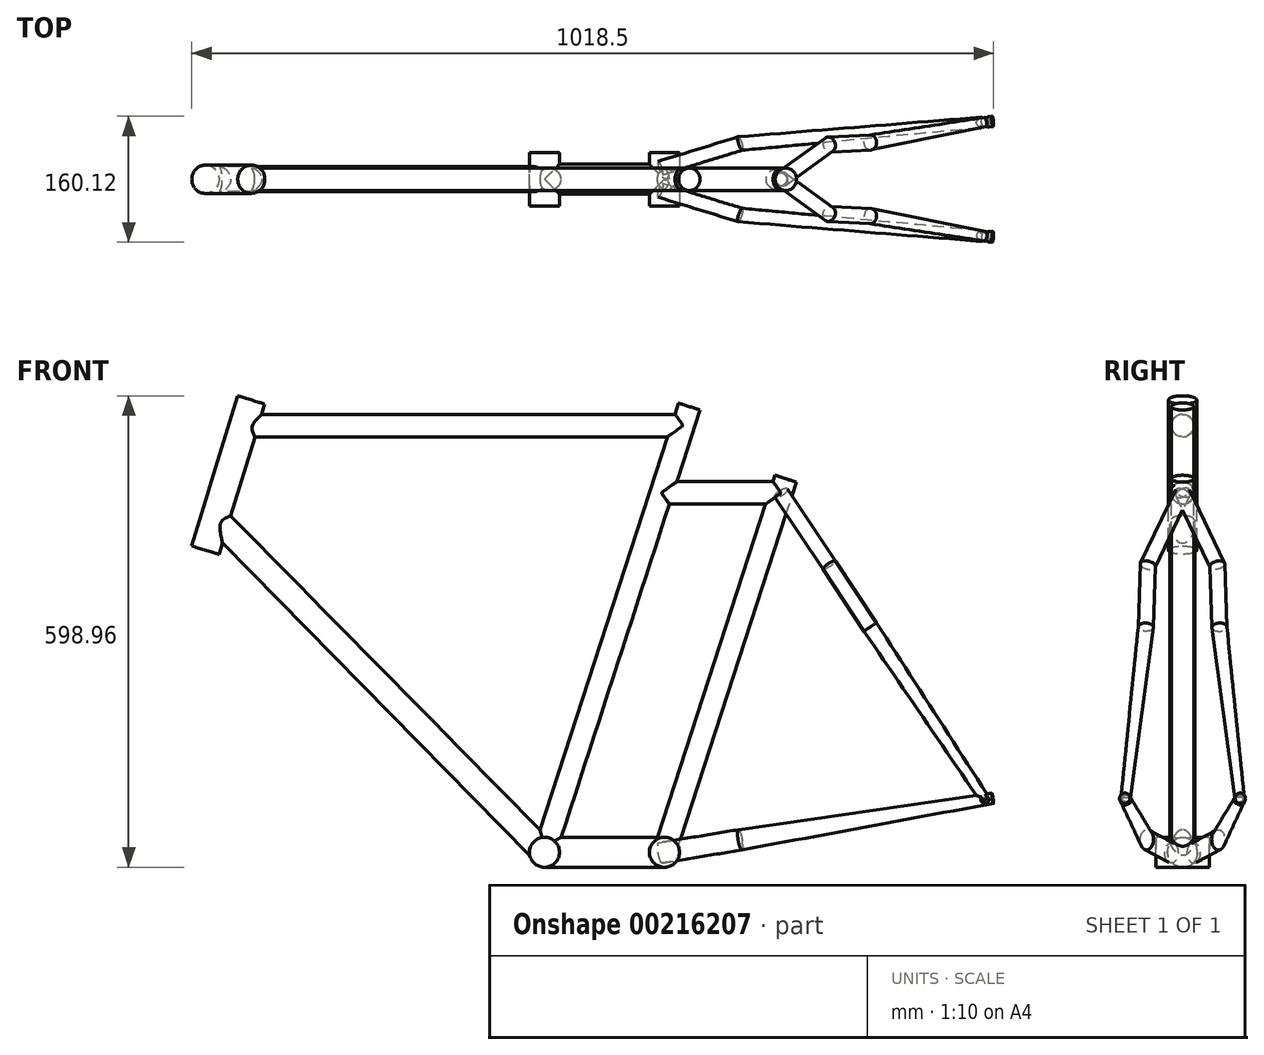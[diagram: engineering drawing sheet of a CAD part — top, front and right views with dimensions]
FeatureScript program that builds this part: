
annotation { "Feature Type Name" : "Feature", "Feature Type Description" : "" }
export const myFeature = defineFeature(function(context is Context, id is Id, definition is map)
    precondition{}
    {
        {
            var Q0;
            Q0=qCreatedBy(makeId("Front.planeOp"),FACE);
            var sketch = newSketch(context, id + "F0", { "sketchPlane" : qUnion([Q0])});
            skLineSegment(sketch, "E0", {"start": v(0, 0) * mm, "end": v(176.14, 542.1) * mm});
            skLineSegment(sketch, "E1", {"start": v(-382.35, 542.09) * mm, "end": v(-527.6, 67) * mm, "construction": true});
            skLineSegment(sketch, "E2.0", {"start": v(1276.12, 67) * mm, "end": v(-807.18, 67) * mm, "construction": true});
            skLineSegment(sketch, "E3", {"start": v(-372.4, 574.65) * mm, "end": v(-430.75, 383.8) * mm});
            skLineSegment(sketch, "E4", {"start": v(0, 0) * mm, "end": v(-418.23, 424.73) * mm});
            skLineSegment(sketch, "E5", {"start": v(300.73, 456.5) * mm, "end": v(152.4, 0) * mm});
            skLineSegment(sketch, "E6", {"start": v(0, 0) * mm, "end": v(152.4, 0) * mm});
            skLineSegment(sketch, "E7", {"start": v(-530.74, -257.5) * mm, "end": v(-876.38, -257.5) * mm, "construction": true});
            skLineSegment(sketch, "E8", {"start": v(-527.6, 67) * mm, "end": v(-626.81, -257.5) * mm});
            skLineSegment(sketch, "E9", {"start": v(-626.81, -257.5) * mm, "end": v(-586.81, -257.5) * mm});
            skLineSegment(sketch, "E10", {"start": v(-586.81, -257.5) * mm, "end": v(-577.2, 67) * mm});
            skPoint(sketch, "E10.endSnap0", {"position": v(-577.2, -95.25) * mm});
            skCircle(sketch, "E11", {"center": v(-577.2, 67) * mm, "radius": 324.63 * mm});
            skLineSegment(sketch, "E12", {"start": v(-577.2, 67) * mm, "end": v(-531.84, 53.13) * mm});
            skCircle(sketch, "E13", {"center": v(559.48, 67) * mm, "radius": 324.63 * mm});
            skLineSegment(sketch, "E14", {"start": v(152.4, 0) * mm, "end": v(559.48, 67) * mm});
            skLineSegment(sketch, "E15", {"start": v(300.73, 456.5) * mm, "end": v(559.48, 67) * mm});
            skLineSegment(sketch, "E16", {"start": v(-382.35, 542.09) * mm, "end": v(176.14, 542.1) * mm});
            skLineSegment(sketch, "E17", {"start": v(300.73, 456.5) * mm, "end": v(148.33, 456.5) * mm});
            skSolve(sketch);
        }
        {
            var Q0;
            Q0=qCreatedBy(makeId("Front.planeOp"),FACE);
            cPlane(context, id + "F1", {"entities" : qUnion([Q0]), "cplaneType" : CPlaneType.OFFSET, "offset" : 34 * mm, "width" : 152.4 * mm, "height" : 152.4 * mm});
        }
        {
            var Q0;
            Q0=qCreatedBy(id+"F1.planeOp",FACE);
            var sketch = newSketch(context, id + "F2", { "sketchPlane" : qUnion([Q0])});
            skCircle(sketch, "E18", {"center": v(0, 0) * mm, "radius": 19.05 * mm});
            skSolve(sketch);
        }
        {
            var Q0;
            Q0=makeQuery(id+"F2.imprint","IMPRINT",FACE,{"disambiguationData":[TD([[makeQuery(id+"F2.imprint","IMPRINT",EDGE,{"derivedFrom":sQuery(id+"F2.wireOp",EDGE,"E18")}),1.0]])]});
            extrude(context, id + "F3", {"entities" : qUnion([Q0]), "oppositeDirection" : true, "depth" : 68 * mm});
        }
        {
            var Q0;
            Q0=qCreatedBy(makeId("Right.planeOp"),FACE);
            var sketch = newSketch(context, id + "F4", { "sketchPlane" : qUnion([Q0])});
            skCircle(sketch, "E19", {"center": v(0, 0) * mm, "radius": 19.05 * mm});
            skSolve(sketch);
        }
        {
            var Q0;
            Q0=qCreatedBy(id+"F1.planeOp",FACE);
            var sketch = newSketch(context, id + "F5", { "sketchPlane" : qUnion([Q0])});
            skCircle(sketch, "E20", {"center": v(152.4, 0) * mm, "radius": 19.05 * mm});
            skSolve(sketch);
        }
        {
            var Q0;
            Q0=makeQuery(id+"F4.imprint","IMPRINT",FACE,{"disambiguationData":[TD([[makeQuery(id+"F4.imprint","IMPRINT",EDGE,{"derivedFrom":sQuery(id+"F4.wireOp",EDGE,"E19")}),1.0]])]});
            var Q1;
            Q1=makeQuery(id+"F7.opExtrude","SWEPT_BODY",BODY,{"disambiguationData":[OSD([sQuery(id+"F5.wireOp",EDGE,"E20")])]});
            extrude(context, id + "F6", {"entities" : qUnion([Q0]), "operationType" : NewBodyOperationType.ADD, "endBoundEntityBody" : qUnion([Q1]), "depth" : 154 * mm});
        }
        {
            var Q0;
            Q0=makeQuery(id+"F5.imprint","IMPRINT",FACE,{"disambiguationData":[TD([[makeQuery(id+"F5.imprint","IMPRINT",EDGE,{"derivedFrom":sQuery(id+"F5.wireOp",EDGE,"E20")}),1.0]])]});
            extrude(context, id + "F7", {"entities" : qUnion([Q0]), "operationType" : NewBodyOperationType.ADD, "oppositeDirection" : true, "depth" : 68 * mm});
        }
        {
            var Q0;
            Q0=sQuery(id+"F0.wireOp",EDGE,"E0");
            var Q1;
            Q1=sQuery(id+"F0.wireOp",VERTEX,"E0.end");
            cPlane(context, id + "F8", {"entities" : qUnion([Q0, Q1]), "cplaneType" : CPlaneType.LINE_POINT, "offset" : 152.4 * mm, "width" : 152.4 * mm, "height" : 152.4 * mm});
        }
        {
            var Q0;
            Q0=qCreatedBy(id+"F8.planeOp",FACE);
            var sketch = newSketch(context, id + "F9", { "sketchPlane" : qUnion([Q0])});
            skCircle(sketch, "E21", {"center": v(0, 0) * mm, "radius": 14.3 * mm});
            skSolve(sketch);
        }
        {
            var Q0;
            Q0=makeQuery(id+"F9.imprint","IMPRINT",FACE,{"disambiguationData":[TD([[makeQuery(id+"F9.imprint","IMPRINT",EDGE,{"derivedFrom":sQuery(id+"F9.wireOp",EDGE,"E21")}),1.0]])]});
            var Q1;
            Q1=makeQuery(id+"F3.opExtrude","SWEPT_BODY",BODY,{"disambiguationData":[OSD([sQuery(id+"F2.wireOp",EDGE,"E18")])]});
            extrude(context, id + "F10", {"entities" : qUnion([Q0]), "operationType" : NewBodyOperationType.ADD, "endBound" : BoundingType.UP_TO_BODY, "oppositeDirection" : true, "endBoundEntityBody" : qUnion([Q1]), "depth" : 25.4 * mm, "hasSecondDirection" : true, "secondDirectionOppositeDirection" : false, "secondDirectionDepth" : 25.4 * mm});
        }
        {
            var Q0;
            Q0=sQuery(id+"F0.wireOp",EDGE,"E14");
            cPlane(context, id + "F11", {"entities" : qUnion([Q0]), "cplaneType" : CPlaneType.LINE_ANGLE, "offset" : 152.4 * mm, "angle" : 90 * degree, "width" : 152.4 * mm, "height" : 152.4 * mm});
        }
        {
            var Q0;
            Q0=qCreatedBy(id+"F11.planeOp",FACE);
            var sketch = newSketch(context, id + "F12", { "sketchPlane" : qUnion([Q0])});
            skLineSegment(sketch, "E22", {"start": v(562.93, 0) * mm, "end": v(562.93, -72.5) * mm});
            skLineSegment(sketch, "E23", {"start": v(562.93, -72.5) * mm, "end": v(247.86, -45.41) * mm});
            skLineSegment(sketch, "E24", {"start": v(247.86, -45.41) * mm, "end": v(145.11, -14.17) * mm});
            skSolve(sketch);
        }
        {
            var Q0;
            Q0=sQuery(id+"F12.wireOp",EDGE,"E23");
            var Q1;
            Q1=sQuery(id+"F12.wireOp",VERTEX,"E23.start");
            cPlane(context, id + "F13", {"entities" : qUnion([Q0, Q1]), "cplaneType" : CPlaneType.LINE_POINT, "offset" : 152.4 * mm, "width" : 152.4 * mm, "height" : 152.4 * mm});
        }
        {
            var Q0;
            Q0=qCreatedBy(id+"F13.planeOp",FACE);
            var sketch = newSketch(context, id + "F14", { "sketchPlane" : qUnion([Q0])});
            skCircle(sketch, "E25", {"center": v(24.02, -24.75) * mm, "radius": 6.73 * mm});
            skSolve(sketch);
        }
        {
            var Q0;
            Q0=sQuery(id+"F12.wireOp",EDGE,"E24");
            var Q1;
            Q1=sQuery(id+"F12.wireOp",VERTEX,"E24.end");
            cPlane(context, id + "F15", {"entities" : qUnion([Q0, Q1]), "cplaneType" : CPlaneType.LINE_POINT, "offset" : 152.4 * mm, "width" : 152.4 * mm, "height" : 152.4 * mm});
        }
        {
            var Q0;
            Q0=qCreatedBy(id+"F15.planeOp",FACE);
            var sketch = newSketch(context, id + "F16", { "sketchPlane" : qUnion([Q0])});
            skEllipse(sketch, "E26", {"center": v(-28.66, -24.75) * mm, "majorRadius": 13.03 * mm, "minorRadius": 8.94 * mm, "majorAxis": v(0, -1)});
            skSolve(sketch);
        }
        {
            var Q0;
            Q0=makeQuery(id+"F16.imprint","IMPRINT",FACE,{"disambiguationData":[TD([[makeQuery(id+"F16.imprint","IMPRINT",EDGE,{"derivedFrom":sQuery(id+"F16.wireOp",EDGE,"E26")}),1.0]])]});
            var Q1;
            Q1=sQuery(id+"F12.wireOp",EDGE,"E24");
            sweep(context, id + "F17", {"profiles" : qUnion([Q0]), "path" : qUnion([Q1])});
        }
        {
            var Q0;
            Q0=qCreatedBy(id+"F11.planeOp",FACE);
            var sketch = newSketch(context, id + "F18", { "sketchPlane" : qUnion([Q0])});
            skLineSegment(sketch, "E27", {"start": v(245.26, -53.97) * mm, "end": v(562.35, -79.2) * mm});
            skSolve(sketch);
        }
        {
            var Q1;
            Q1=makeQuery(id+"F17.opSweep","CAP_FACE",FACE,{"disambiguationData":[OSD([sQuery(id+"F12.wireOp",VERTEX,"E24.start"),sQuery(id+"F16.wireOp",EDGE,"E26")])],"isStart":false});
            var Q2;
            Q2=makeQuery(id+"F14.imprint","IMPRINT",FACE,{"disambiguationData":[TD([[makeQuery(id+"F14.imprint","IMPRINT",EDGE,{"derivedFrom":sQuery(id+"F14.wireOp",EDGE,"E25")}),1.0]])]});
            var Q3;
            Q3=sQuery(id+"F18.wireOp",EDGE,"E27");
            loft(context, id + "F19", {"operationType" : NewBodyOperationType.ADD, "addGuides" : true, "sheetProfilesArray" : [{ "sheetProfileEntities" : qUnion([Q1]) }, { "sheetProfileEntities" : qUnion([Q2]) }], "guidesArray" : [{ "guideEntities" : qUnion([Q3]), "guideDerivativeType" : LoftGuideDerivativeType.DEFAULT, "guideDerivativeMagnitude" : 1 }]});
        }
        {
            var Q0;
            Q0=makeQuery(id+"F19.opLoft","CAP_FACE",FACE,{"disambiguationData":[OSD([makeQuery(id+"F14.imprint","IMPRINT",FACE,{"disambiguationData":[TD([[makeQuery(id+"F14.imprint","IMPRINT",EDGE,{"derivedFrom":sQuery(id+"F14.wireOp",EDGE,"E25")}),1.0]])]})])],"isStart":true});
            extrude(context, id + "F20", {"entities" : qUnion([Q0]), "operationType" : NewBodyOperationType.ADD, "depth" : 10 * mm});
        }
        {
            var Q0;
            Q0=qCreatedBy(makeId("Front.planeOp"),FACE);
            var sketch = newSketch(context, id + "F21", { "sketchPlane" : qUnion([Q0])});
            skCircle(sketch, "E28", {"center": v(559.48, 67) * mm, "radius": 5 * mm});
            skSolve(sketch);
        }
        {
            var Q0;
            Q0=makeQuery(id+"F21.imprint","IMPRINT",FACE,{"disambiguationData":[TD([[makeQuery(id+"F21.imprint","IMPRINT",EDGE,{"derivedFrom":sQuery(id+"F21.wireOp",EDGE,"E28")}),1.0]])]});
            var Q1;
            Q1=sQuery(id+"F21.wireOp",EDGE,"E28");
            extrude(context, id + "F22", {"entities" : qUnion([Q0]), "surfaceEntities" : qUnion([Q1]), "depth" : 84.17 * mm});
        }
        {
            var Q0;
            Q0=makeQuery(id+"F22.opExtrude","SWEPT_BODY",BODY,{"disambiguationData":[OSD([sQuery(id+"F21.wireOp",EDGE,"E28")])]});
            var Q1;
            Q1=makeQuery(id+"F17.opSweep","SWEPT_BODY",BODY,{"disambiguationData":[OSD([sQuery(id+"F12.wireOp",EDGE,"E24"),sQuery(id+"F16.wireOp",EDGE,"E26")])]});
            booleanBodies(context, id + "F23", {"operationType" : BooleanOperationType.SUBTRACTION, "tools" : qUnion([Q0]), "targets" : qUnion([Q1])});
        }
        {
            var Q0;
            Q0=sQuery(id+"F0.wireOp",EDGE,"E5");
            var Q1;
            Q1=sQuery(id+"F0.wireOp",VERTEX,"E15.start");
            cPlane(context, id + "F24", {"entities" : qUnion([Q0, Q1]), "cplaneType" : CPlaneType.LINE_POINT, "offset" : 152.4 * mm, "width" : 152.4 * mm, "height" : 152.4 * mm});
        }
        {
            var Q0;
            Q0=qCreatedBy(id+"F24.planeOp",FACE);
            var sketch = newSketch(context, id + "F25", { "sketchPlane" : qUnion([Q0])});
            skCircle(sketch, "E29", {"center": v(144.94, 0) * mm, "radius": 14.3 * mm});
            skSolve(sketch);
        }
        {
            var Q0;
            Q0=makeQuery(id+"F25.imprint","IMPRINT",FACE,{"disambiguationData":[TD([[makeQuery(id+"F25.imprint","IMPRINT",EDGE,{"derivedFrom":sQuery(id+"F25.wireOp",EDGE,"E29")}),1.0]])]});
            var Q1;
            Q1=makeQuery(id+"F3.opExtrude","SWEPT_BODY",BODY,{"disambiguationData":[OSD([sQuery(id+"F2.wireOp",EDGE,"E18")])]});
            extrude(context, id + "F26", {"entities" : qUnion([Q0]), "operationType" : NewBodyOperationType.ADD, "endBound" : BoundingType.UP_TO_BODY, "endBoundEntityBody" : qUnion([Q1]), "depth" : 25.4 * mm, "hasSecondDirection" : true, "secondDirectionOppositeDirection" : true, "secondDirectionDepth" : 19 * mm});
        }
        {
            var Q0;
            Q0=sQuery(id+"F0.wireOp",EDGE,"E4");
            var Q1;
            Q1=sQuery(id+"F0.wireOp",VERTEX,"E4.end");
            cPlane(context, id + "F27", {"entities" : qUnion([Q0, Q1]), "cplaneType" : CPlaneType.LINE_POINT, "offset" : 152.4 * mm, "width" : 152.4 * mm, "height" : 152.4 * mm});
        }
        {
            var Q0;
            Q0=qCreatedBy(id+"F27.planeOp",FACE);
            var sketch = newSketch(context, id + "F28", { "sketchPlane" : qUnion([Q0])});
            skCircle(sketch, "E30", {"center": v(0, 0) * mm, "radius": 15.9 * mm});
            skSolve(sketch);
        }
        {
            var Q0;
            Q0=makeQuery(id+"F28.imprint","IMPRINT",FACE,{"disambiguationData":[TD([[makeQuery(id+"F28.imprint","IMPRINT",EDGE,{"derivedFrom":sQuery(id+"F28.wireOp",EDGE,"E30")}),1.0]])]});
            var Q1;
            Q1=makeQuery(id+"F3.opExtrude","SWEPT_BODY",BODY,{"disambiguationData":[OSD([sQuery(id+"F2.wireOp",EDGE,"E18")])]});
            extrude(context, id + "F29", {"entities" : qUnion([Q0]), "operationType" : NewBodyOperationType.ADD, "endBound" : BoundingType.UP_TO_BODY, "oppositeDirection" : true, "endBoundEntityBody" : qUnion([Q1]), "depth" : 25.4 * mm});
        }
        {
            var Q0;
            Q0=sQuery(id+"F0.wireOp",EDGE,"E3");
            var Q1;
            Q1=sQuery(id+"F0.wireOp",VERTEX,"E3.start");
            cPlane(context, id + "F30", {"entities" : qUnion([Q0, Q1]), "cplaneType" : CPlaneType.LINE_POINT, "offset" : 152.4 * mm, "width" : 152.4 * mm, "height" : 152.4 * mm});
        }
        {
            var Q0;
            Q0=qCreatedBy(id+"F30.planeOp",FACE);
            var sketch = newSketch(context, id + "F31", { "sketchPlane" : qUnion([Q0])});
            skCircle(sketch, "E31", {"center": v(-524.14, 0) * mm, "radius": 18 * mm});
            skSolve(sketch);
        }
        {
            var Q0;
            Q0=sQuery(id+"F0.wireOp",EDGE,"E15");
            cPlane(context, id + "F32", {"entities" : qUnion([Q0]), "cplaneType" : CPlaneType.LINE_ANGLE, "offset" : 152.4 * mm, "angle" : 0 * degree, "width" : 152.4 * mm, "height" : 152.4 * mm});
        }
        {
            var Q0;
            Q0=qCreatedBy(id+"F32.planeOp",FACE);
            var sketch = newSketch(context, id + "F33", { "sketchPlane" : qUnion([Q0])});
            skLineSegment(sketch, "E32", {"start": v(72.5, -253.77) * mm, "end": v(46.8, 9.14) * mm});
            skLineSegment(sketch, "E33", {"start": v(46.8, 9.14) * mm, "end": v(44.18, 103.87) * mm});
            skLineSegment(sketch, "E34", {"start": v(44.18, 103.87) * mm, "end": v(0, 213.85) * mm});
            skSolve(sketch);
        }
        {
            var Q0;
            Q0=sQuery(id+"F33.wireOp",EDGE,"E34");
            var Q1;
            Q1=sQuery(id+"F33.wireOp",VERTEX,"E34.end");
            cPlane(context, id + "F34", {"entities" : qUnion([Q0, Q1]), "cplaneType" : CPlaneType.LINE_POINT, "offset" : 152.4 * mm, "width" : 152.4 * mm, "height" : 152.4 * mm});
        }
        {
            var Q0;
            Q0=qCreatedBy(id+"F34.planeOp",FACE);
            var sketch = newSketch(context, id + "F35", { "sketchPlane" : qUnion([Q0])});
            skCircle(sketch, "E35", {"center": v(469.2, -198.29) * mm, "radius": 9.53 * mm});
            skSolve(sketch);
        }
        {
            var Q0;
            Q0=makeQuery(id+"F35.imprint","IMPRINT",FACE,{"disambiguationData":[TD([[makeQuery(id+"F35.imprint","IMPRINT",EDGE,{"derivedFrom":sQuery(id+"F35.wireOp",EDGE,"E35")}),1.0]])]});
            var Q1;
            Q1=sQuery(id+"F33.wireOp",EDGE,"E34");
            var Q2;
            Q2=sQuery(id+"F33.wireOp",EDGE,"E33");
            sweep(context, id + "F36", {"profiles" : qUnion([Q0]), "path" : qUnion([Q1, Q2])});
        }
        {
            var Q0;
            Q0=sQuery(id+"F33.wireOp",VERTEX,"E32.start");
            var Q1;
            Q1=sQuery(id+"F33.wireOp",EDGE,"E32");
            cPlane(context, id + "F37", {"entities" : qUnion([Q0, Q1]), "cplaneType" : CPlaneType.LINE_POINT, "offset" : 152.4 * mm, "width" : 152.4 * mm, "height" : 152.4 * mm});
        }
        {
            var Q0;
            Q0=qCreatedBy(id+"F37.planeOp",FACE);
            var sketch = newSketch(context, id + "F38", { "sketchPlane" : qUnion([Q0])});
            skCircle(sketch, "E36", {"center": v(498.99, -79.82) * mm, "radius": 6 * mm});
            skSolve(sketch);
        }
        {
            var Q1;
            Q1=makeQuery(id+"F36.opSweep","CAP_FACE",FACE,{"disambiguationData":[OSD([sQuery(id+"F33.wireOp",VERTEX,"E33.start"),sQuery(id+"F35.wireOp",EDGE,"E35")])],"isStart":false});
            var Q2;
            Q2=makeQuery(id+"F38.imprint","IMPRINT",FACE,{"disambiguationData":[TD([[makeQuery(id+"F38.imprint","IMPRINT",EDGE,{"derivedFrom":sQuery(id+"F38.wireOp",EDGE,"E36")}),1.0]])]});
            loft(context, id + "F39", {"operationType" : NewBodyOperationType.ADD, "sheetProfilesArray" : [{ "sheetProfileEntities" : qUnion([Q1]) }, { "sheetProfileEntities" : qUnion([Q2]) }]});
        }
        {
            var Q0;
            Q0=makeQuery(id+"F31.imprint","IMPRINT",FACE,{"disambiguationData":[TD([[makeQuery(id+"F31.imprint","IMPRINT",EDGE,{"derivedFrom":sQuery(id+"F31.wireOp",EDGE,"E31")}),1.0]])]});
            var Q1;
            Q1=sQuery(id+"F31.wireOp",EDGE,"E31");
            var Q2;
            Q2=sQuery(id+"F0.wireOp",VERTEX,"E3.end");
            extrude(context, id + "F40", {"entities" : qUnion([Q0]), "operationType" : NewBodyOperationType.ADD, "surfaceEntities" : qUnion([Q1]), "endBound" : BoundingType.UP_TO_VERTEX, "endBoundEntityVertex" : qUnion([Q2]), "depth" : 199 * mm});
        }
        {
            var Q0;
            Q0=sQuery(id+"F0.wireOp",VERTEX,"E16.start");
            var Q1;
            Q1=sQuery(id+"F0.wireOp",EDGE,"E16");
            cPlane(context, id + "F41", {"entities" : qUnion([Q0, Q1]), "cplaneType" : CPlaneType.LINE_POINT, "offset" : 25 * mm, "width" : 150 * mm, "height" : 150 * mm});
        }
        {
            var Q0;
            Q0=qCreatedBy(id+"F41.planeOp",FACE);
            var sketch = newSketch(context, id + "F42", { "sketchPlane" : qUnion([Q0])});
            skCircle(sketch, "E37", {"center": v(0, 542.1) * mm, "radius": 14.29 * mm});
            skSolve(sketch);
        }
        {
            var Q0;
            Q0 = qSketchRegion(id + "F42", true);
            var Q1;
            Q1=makeQuery(id+"F10.opExtrude","SWEPT_FACE",FACE,{"disambiguationData":[OSD([sQuery(id+"F9.wireOp",EDGE,"E21")])]});
            var Q2;
            Q2=makeQuery(id+"F3.opExtrude","SWEPT_BODY",BODY,{"disambiguationData":[OSD([sQuery(id+"F2.wireOp",EDGE,"E18")])]});
            extrude(context, id + "F43", {"entities" : qUnion([Q0]), "operationType" : NewBodyOperationType.ADD, "endBound" : BoundingType.UP_TO_SURFACE, "endBoundEntityFace" : qUnion([Q1]), "endBoundEntityBody" : qUnion([Q2]), "depth" : 25 * mm});
        }
        {
            var Q0;
            Q0=sQuery(id+"F0.wireOp",EDGE,"E17");
            var Q1;
            Q1=sQuery(id+"F0.wireOp",VERTEX,"E17.end");
            cPlane(context, id + "F44", {"entities" : qUnion([Q0, Q1]), "cplaneType" : CPlaneType.LINE_POINT, "offset" : 25 * mm, "width" : 150 * mm, "height" : 150 * mm});
        }
        {
            var Q0;
            Q0=qCreatedBy(id+"F44.planeOp",FACE);
            var sketch = newSketch(context, id + "F45", { "sketchPlane" : qUnion([Q0])});
            skCircle(sketch, "E38", {"center": v(0, 456.5) * mm, "radius": 14.29 * mm});
            skSolve(sketch);
        }
        {
            var Q0;
            Q0 = qSketchRegion(id + "F45", true);
            var Q1;
            Q1=makeQuery(id+"F26.opExtrude","SWEPT_FACE",FACE,{"disambiguationData":[OSD([sQuery(id+"F25.wireOp",EDGE,"E29")])]});
            var Q2;
            Q2=makeQuery(id+"F3.opExtrude","SWEPT_BODY",BODY,{"disambiguationData":[OSD([sQuery(id+"F2.wireOp",EDGE,"E18")])]});
            extrude(context, id + "F46", {"entities" : qUnion([Q0]), "operationType" : NewBodyOperationType.ADD, "endBound" : BoundingType.UP_TO_SURFACE, "oppositeDirection" : true, "endBoundEntityFace" : qUnion([Q1]), "endBoundEntityBody" : qUnion([Q2]), "depth" : 25 * mm});
        }
        {
            var Q0;
            Q0=makeQuery(id+"F17.opSweep","SWEPT_BODY",BODY,{"disambiguationData":[OSD([sQuery(id+"F12.wireOp",EDGE,"E24"),sQuery(id+"F16.wireOp",EDGE,"E26")])]});
            var Q1;
            Q1=makeQuery(id+"F36.opSweep","SWEPT_BODY",BODY,{"disambiguationData":[OSD([sQuery(id+"F33.wireOp",EDGE,"E33"),sQuery(id+"F35.wireOp",EDGE,"E35")])]});
            var Q2;
            Q2=qCreatedBy(makeId("Front.planeOp"),FACE);
            mirror(context, id + "F47", {"entities" : qUnion([Q0, Q1]), "mirrorPlane" : qUnion([Q2])});
        }
    });
